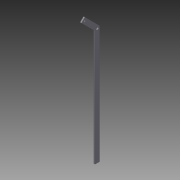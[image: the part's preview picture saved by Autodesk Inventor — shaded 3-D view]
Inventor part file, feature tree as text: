
AUTODESK INVENTOR PART (.ipt)
format: ipt  version: 2014 SP1 (Build 180222100, 222)  size: 80,896 bytes
history: native  units: in
note: dims shown in document units (in); Inventor stores cm internally (conversion verified against a paired STEP export)
features: extrude x1, sketch x1
ambient origin geometry x8: Origin, YZ Plane, XZ Plane, XY Plane, X Axis, Y Axis, Z Axis, Center Point
bodies: Solid1 (feature_tree)
feature tree (2):
  extrude  "Extrusion1"  Depth=0.25in
  sketch  "Sketch1"  dims[d0=1.0in d7=24.0in d8=4.0in d9=135.0deg d10=1.0in d11=0.5in d12=0.25in d13=0.5in d14=0.5in d15=0.25in d16=0.0in]
